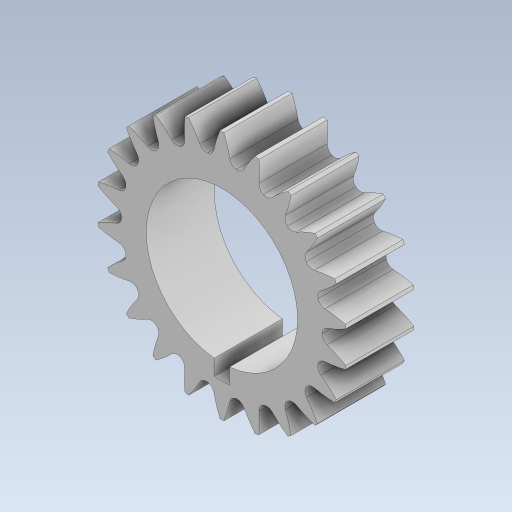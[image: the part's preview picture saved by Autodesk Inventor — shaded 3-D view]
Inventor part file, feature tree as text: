
AUTODESK INVENTOR PART (.ipt)
format: ipt  version: 2023.5 (Build 275446000, 446)  size: 272,384 bytes
history: native  units: in
note: dims shown in document units (in); Inventor stores cm internally (conversion verified against a paired STEP export)
features: extrude x2, sketch x1, fillet x1, pattern_circular x1
ambient origin geometry x8: Origin, YZ Plane, XZ Plane, XY Plane, X Axis, Y Axis, Z Axis, Center Point
bodies: Body1 (feature_tree)
feature tree (5):
  sketch  "Sketch1"  dims[d0=0.7874in d3=1.1811in d4=1.2992in d5=1.0433in d17=0.0394in d20=0.0618in d23=0.0925in d24=0.0197in d25=0.3543in d26=0.0in d27=0.3543in d28=0.0in d29=0.0394in d30=8.6614in d31=360.0deg d12=0.0197in d13=0.0344in d14=0.0197in d15=0.0344in]
  extrude  "Extrusion3"  Depth=0.0394in
  extrude  "Extrusion4"  Depth=0.0394in
  fillet  "Fillet2"  Radius=1.0433in
  pattern_circular  "Circular Pattern1"  [2 undecoded]
note: 2 required parameter values undecoded (feature->parameter linkage not recoverable at this tier; creation-order binding heuristic only, values carry confidence <= 0.55)
